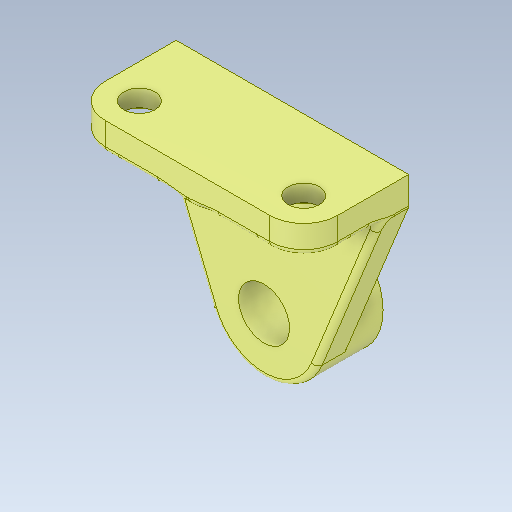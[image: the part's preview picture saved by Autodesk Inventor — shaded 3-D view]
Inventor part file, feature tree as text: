
AUTODESK INVENTOR PART (.ipt)
format: ipt  version: 2020 (Build 240168000, 168)  size: 323,072 bytes
history: native  units: mm
features: extrude x5, sketch x4, fillet x2, plane x1, rib x1
ambient origin geometry x8: Origin, YZ Plane, XZ Plane, XY Plane, X Axis, Y Axis, Z Axis, Center Point
bodies: Solid1 (feature_tree)
feature tree (13):
  extrude  "Extrusion1"  Depth=41.0mm
  sketch  "Sketch2"  dims[d2=18.0mm d3=22.0mm d4=0.0mm]
  extrude  "Extrusion2"  Depth=22.0mm TaperAngle=0.0deg
  extrude  "Extrusion3"  Depth=41.0mm
  plane  "Work Plane1"
  rib  "Rib1"
  sketch  "Sketch6"  dims[d7=10.0mm d8=10.0mm d9=0.0mm d10=27.0mm d11=0.0mm d12=-41.0mm d17=1.0mm d18=10.0mm d19=0.0mm d20=0.0mm d21=1.0mm d22=1.0mm d23=11.0mm d24=22.0mm d25=22.0mm d26=11.0mm d27=12.0mm d28=12.0mm d29=12.0mm d30=12.0mm d31=27.0mm d32=0.0mm d33=4.0mm d34=0.0mm d35=12.0mm d37=2.0mm]
  extrude  "Extrusion4"  Depth=10.0mm TaperAngle=0.0deg
  extrude  "Extrusion5"  Depth=27.0mm TaperAngle=0.0deg
  fillet  "Fillet1"  [1 undecoded]
  fillet  "Fillet3"  Radius=1.0mm
  sketch  "Sketch1"  dims[d0=40.0mm d1=41.0mm]
  sketch  "Sketch5"  dims[d5=82.0mm d6=41.0mm]
note: 1 required parameter value undecoded (feature->parameter linkage not recoverable at this tier; creation-order binding heuristic only, values carry confidence <= 0.55)
